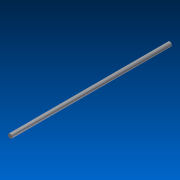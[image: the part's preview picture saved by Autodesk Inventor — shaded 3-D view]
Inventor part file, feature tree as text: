
AUTODESK INVENTOR PART (.ipt)
format: ipt  version: 2012 (Build 160160000, 160)  size: 63,488 bytes
history: native  units: in
note: dims shown in document units (in); Inventor stores cm internally (conversion verified against a paired STEP export)
features: extrude x1, sketch x1
ambient origin geometry x8: Origin, YZ Plane, XZ Plane, XY Plane, X Axis, Y Axis, Z Axis, Center Point
bodies: Solid1 (feature_tree)
feature tree (2):
  extrude  "Extrusion1"  Depth=3.6417in TaperAngle=0.0deg
  sketch  "Sketch1"  dims[d0=0.0984in d1=3.6417in d2=0.0in]
